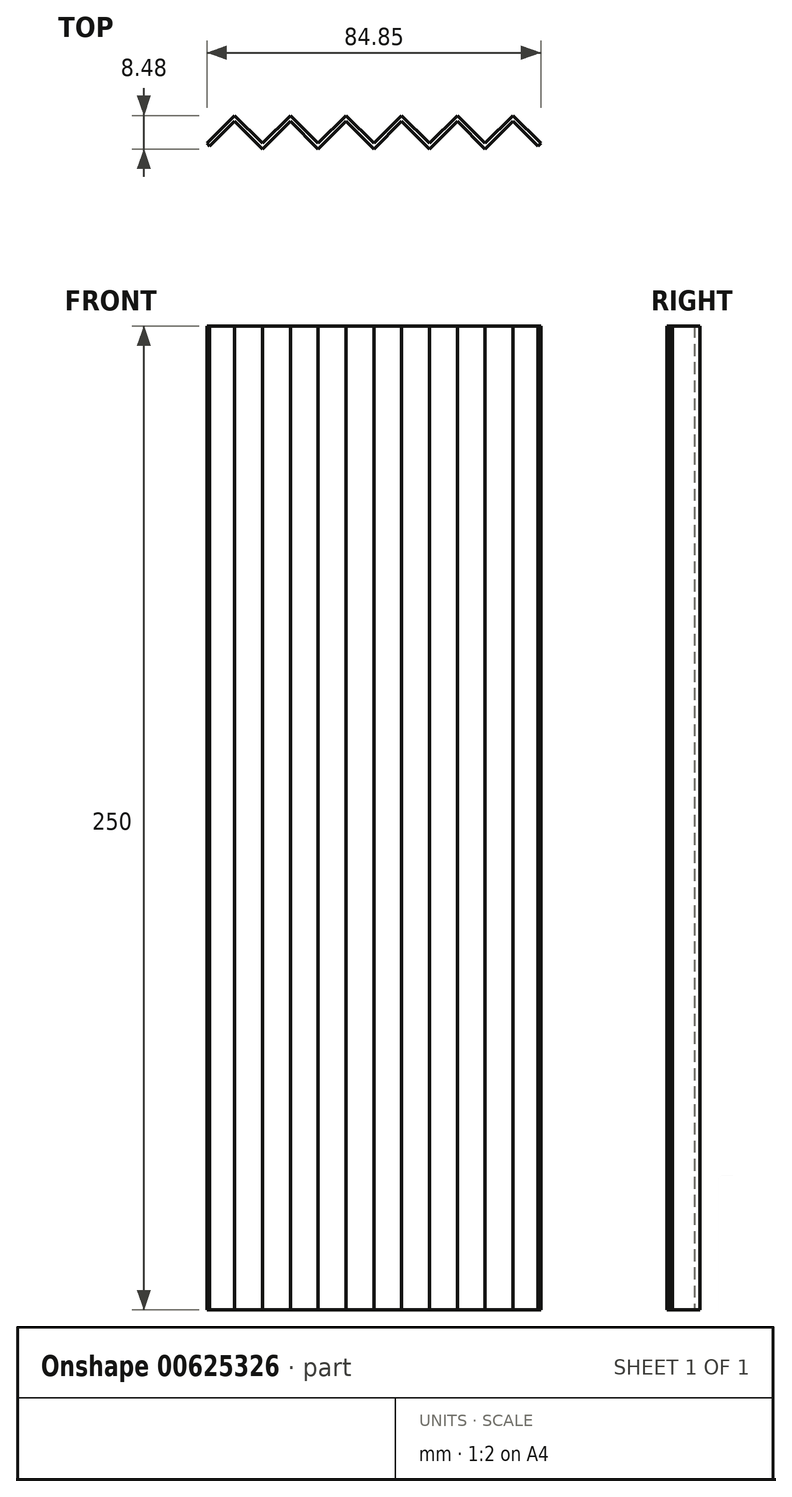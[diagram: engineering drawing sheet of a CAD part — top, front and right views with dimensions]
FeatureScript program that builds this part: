
annotation { "Feature Type Name" : "Feature", "Feature Type Description" : "" }
export const myFeature = defineFeature(function(context is Context, id is Id, definition is map)
    precondition{}
    {
        {
            var Q0;
            Q0=qCreatedBy(makeId("Top.planeOp"),FACE);
            var sketch = newSketch(context, id + "F0", { "sketchPlane" : qUnion([Q0])});
            skLineSegment(sketch, "E0", {"start": v(-53.48, 0) * mm, "end": v(-46.41, 7.07) * mm});
            skLineSegment(sketch, "E1", {"start": v(-46.41, 7.07) * mm, "end": v(-39.34, 0) * mm});
            skLineSegment(sketch, "E2", {"start": v(-39.34, 0) * mm, "end": v(-32.27, 7.07) * mm});
            skLineSegment(sketch, "E3", {"start": v(-32.27, 7.07) * mm, "end": v(-25.2, 0) * mm});
            skLineSegment(sketch, "E4", {"start": v(-25.2, 0) * mm, "end": v(-18.13, 7.07) * mm});
            skLineSegment(sketch, "E5", {"start": v(-18.13, 7.07) * mm, "end": v(-11.06, 0) * mm});
            skLineSegment(sketch, "E6", {"start": v(-11.06, 0) * mm, "end": v(-3.98, 7.07) * mm});
            skLineSegment(sketch, "E7", {"start": v(-3.98, 7.07) * mm, "end": v(3.09, 0) * mm});
            skLineSegment(sketch, "E8", {"start": v(3.09, 0) * mm, "end": v(3.09, 0) * mm});
            skLineSegment(sketch, "E9", {"start": v(3.09, 0) * mm, "end": v(10.16, 7.07) * mm});
            skLineSegment(sketch, "E10", {"start": v(10.16, 7.07) * mm, "end": v(17.23, 0) * mm});
            skLineSegment(sketch, "E11", {"start": v(17.23, 0) * mm, "end": v(24.3, 7.07) * mm});
            skLineSegment(sketch, "E12", {"start": v(24.3, 7.07) * mm, "end": v(31.37, 0) * mm});
            skLineSegment(sketch, "E13.0", {"start": v(24.3, 5.66) * mm, "end": v(30.66, -0.7) * mm});
            skLineSegment(sketch, "E13.1", {"start": v(17.23, -1.41) * mm, "end": v(24.3, 5.66) * mm});
            skLineSegment(sketch, "E13.2", {"start": v(-32.27, 5.66) * mm, "end": v(-25.2, -1.41) * mm});
            skLineSegment(sketch, "E13.3", {"start": v(-39.34, -1.41) * mm, "end": v(-32.27, 5.66) * mm});
            skLineSegment(sketch, "E13.4", {"start": v(-46.41, 5.66) * mm, "end": v(-39.34, -1.41) * mm});
            skLineSegment(sketch, "E13.5", {"start": v(-52.77, -0.7) * mm, "end": v(-46.41, 5.66) * mm});
            skLineSegment(sketch, "E13.6", {"start": v(-25.2, -1.41) * mm, "end": v(-18.13, 5.66) * mm});
            skLineSegment(sketch, "E13.7", {"start": v(-18.13, 5.66) * mm, "end": v(-11.06, -1.41) * mm});
            skLineSegment(sketch, "E13.8", {"start": v(-11.06, -1.41) * mm, "end": v(-3.98, 5.66) * mm});
            skLineSegment(sketch, "E13.9", {"start": v(-3.98, 5.66) * mm, "end": v(3.09, -1.41) * mm});
            skLineSegment(sketch, "E13.10", {"start": v(3.09, -1.41) * mm, "end": v(10.16, 5.66) * mm});
            skLineSegment(sketch, "E13.11", {"start": v(10.16, 5.66) * mm, "end": v(17.23, -1.41) * mm});
            skLineSegment(sketch, "E14", {"start": v(31.37, 0) * mm, "end": v(30.66, -0.7) * mm});
            skLineSegment(sketch, "E15", {"start": v(-53.48, 0) * mm, "end": v(-52.77, -0.7) * mm});
            skSolve(sketch);
        }
        {
            var Q0;
            Q0 = qSketchRegion(id + "F0", true);
            extrude(context, id + "F1", {"entities" : qUnion([Q0]), "depth" : 250 * mm, "offsetDistance" : 25 * mm});
        }
    });
